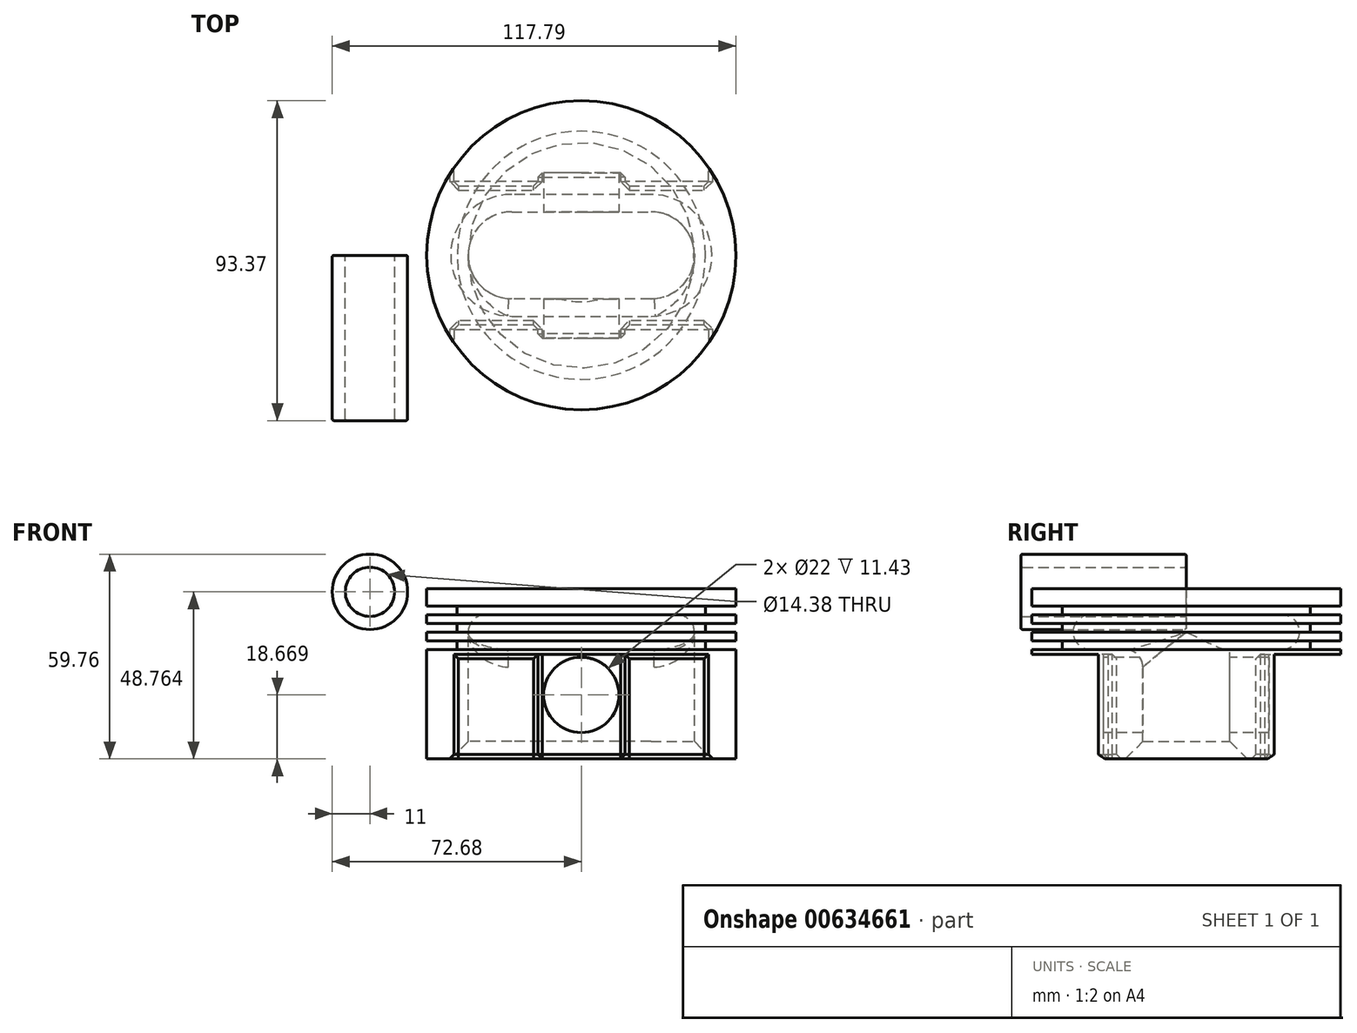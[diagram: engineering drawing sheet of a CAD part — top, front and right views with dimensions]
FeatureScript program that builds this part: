
annotation { "Feature Type Name" : "Feature", "Feature Type Description" : "" }
export const myFeature = defineFeature(function(context is Context, id is Id, definition is map)
    precondition{}
    {
        {
            var Q0;
            Q0=qCreatedBy(makeId("Front.planeOp"),FACE);
            var sketch = newSketch(context, id + "F0", { "sketchPlane" : qUnion([Q0])});
            skLineSegment(sketch, "E0", {"start": v(0, 30.06) * mm, "end": v(-45.11, 30.06) * mm});
            skLineSegment(sketch, "E1", {"start": v(-45.11, 30.06) * mm, "end": v(-45.11, 24.98) * mm});
            skLineSegment(sketch, "E2", {"start": v(-45.11, 24.98) * mm, "end": v(-36.22, 24.98) * mm});
            skLineSegment(sketch, "E3", {"start": v(-36.22, 24.98) * mm, "end": v(-36.22, 22.44) * mm});
            skLineSegment(sketch, "E4", {"start": v(-36.22, 22.44) * mm, "end": v(-45.11, 22.44) * mm});
            skLineSegment(sketch, "E5", {"start": v(-45.11, 22.44) * mm, "end": v(-45.11, 19.9) * mm});
            skLineSegment(sketch, "E6", {"start": v(-45.11, 19.9) * mm, "end": v(-36.22, 19.9) * mm});
            skLineSegment(sketch, "E7", {"start": v(-36.22, 19.9) * mm, "end": v(-36.22, 17.36) * mm});
            skLineSegment(sketch, "E8", {"start": v(-36.22, 17.36) * mm, "end": v(-45.11, 17.36) * mm});
            skLineSegment(sketch, "E9", {"start": v(-45.11, 17.36) * mm, "end": v(-45.11, 14.82) * mm});
            skLineSegment(sketch, "E10", {"start": v(-45.11, 14.82) * mm, "end": v(-36.22, 14.82) * mm});
            skLineSegment(sketch, "E11", {"start": v(-45.11, 10.86) * mm, "end": v(-45.11, -0.67) * mm});
            skLineSegment(sketch, "E12", {"start": v(-45.11, 10.86) * mm, "end": v(0, 10.86) * mm});
            skLineSegment(sketch, "E13", {"start": v(-36.22, 14.82) * mm, "end": v(-36.22, 12.28) * mm});
            skLineSegment(sketch, "E14", {"start": v(-36.22, 12.28) * mm, "end": v(-45.11, 12.28) * mm});
            skLineSegment(sketch, "E15", {"start": v(-45.11, 12.28) * mm, "end": v(-45.11, 10.86) * mm});
            skLineSegment(sketch, "E16", {"start": v(0, 30.06) * mm, "end": v(0, 22.44) * mm});
            skLineSegment(sketch, "E17", {"start": v(0, 22.44) * mm, "end": v(-27.94, 22.44) * mm});
            skLineSegment(sketch, "E18", {"start": v(0, 0) * mm, "end": v(0, 12.28) * mm});
            skLineSegment(sketch, "E19", {"start": v(0, 12.28) * mm, "end": v(-27.94, 12.28) * mm});
            skArc(sketch, "E20", {"start": v(-27.94, 22.44) * mm, "mid": v(-33.02, 17.36) * mm, "end": v(-27.94, 12.28) * mm});
            skLineSegment(sketch, "E21", {"start": v(0, 0.32) * mm, "end": v(0, 10.86) * mm});
            skCircle(sketch, "E22", {"center": v(0, -0.95) * mm, "radius": 11 * mm, "construction": true});
            skSolve(sketch);
        }
        {
            var Q0;
            Q0=makeQuery(id+"F0.imprint","IMPRINT",FACE,{"disambiguationData":[TD([[makeQuery(id+"F0.imprint","IMPRINT",EDGE,{"derivedFrom":sQuery(id+"F0.wireOp",EDGE,"E0")}),1.0]])]});
            var Q1;
            Q1=sQuery(id+"F0.wireOp",EDGE,"E18");
            revolve(context, id + "F1", {"entities" : qUnion([Q0]), "axis" : qUnion([Q1]), "revolveType" : RevolveType.FULL});
        }
        {
            var Q0;
            Q0=makeQuery(id+"F1.opRevolve","SWEPT_FACE",FACE,{"disambiguationData":[OSD([sQuery(id+"F0.wireOp",EDGE,"E12")])]});
            var sketch = newSketch(context, id + "F2", { "sketchPlane" : qUnion([Q0])});
            skLineSegment(sketch, "E23", {"start": v(0, 12.7) * mm, "end": v(-20.32, 12.7) * mm});
            skLineSegment(sketch, "E24.MirrorCS", {"start": v(0, -12.7) * mm, "end": v(-20.32, -12.7) * mm});
            skArc(sketch, "E25", {"start": v(-20.32, 12.7) * mm, "mid": v(-33.02, 0) * mm, "end": v(-20.32, -12.7) * mm});
            skLineSegment(sketch, "E26.MirrorCS", {"start": v(0, 12.7) * mm, "end": v(20.32, 12.7) * mm});
            skArc(sketch, "E27.MirrorCS", {"start": v(20.32, 12.7) * mm, "mid": v(33.02, 0) * mm, "end": v(20.32, -12.7) * mm});
            skLineSegment(sketch, "E28.MirrorCS", {"start": v(0, -12.7) * mm, "end": v(20.32, -12.7) * mm});
            skLineSegment(sketch, "E29", {"start": v(-12.7, 20.32) * mm, "end": v(-37.13, 20.32) * mm});
            skLineSegment(sketch, "E30", {"start": v(-37.13, 20.32) * mm, "end": v(-37.13, 25.61) * mm});
            skLineSegment(sketch, "E31", {"start": v(0, 24.13) * mm, "end": v(-12.7, 24.13) * mm});
            skLineSegment(sketch, "E32", {"start": v(-12.7, 24.13) * mm, "end": v(-12.7, 20.32) * mm});
            skPoint(sketch, "E33.orphan", {"position": v(0, 20.32) * mm});
            skLineSegment(sketch, "E34.MirrorCS", {"start": v(12.7, 24.13) * mm, "end": v(12.7, 20.32) * mm});
            skLineSegment(sketch, "E35.MirrorCS", {"start": v(37.13, 20.32) * mm, "end": v(37.13, 25.61) * mm});
            skLineSegment(sketch, "E36.MirrorCS", {"start": v(0, 24.13) * mm, "end": v(12.7, 24.13) * mm});
            skLineSegment(sketch, "E37.MirrorCS", {"start": v(12.7, 20.32) * mm, "end": v(37.13, 20.32) * mm});
            skLineSegment(sketch, "E38.MirrorCS", {"start": v(12.7, -24.13) * mm, "end": v(12.7, -20.32) * mm});
            skLineSegment(sketch, "E39.MirrorCS", {"start": v(-12.7, -24.13) * mm, "end": v(-12.7, -20.32) * mm});
            skPoint(sketch, "E40.MirrorP", {"position": v(0, -20.32) * mm});
            skLineSegment(sketch, "E41.MirrorCS", {"start": v(-12.7, -20.32) * mm, "end": v(-37.13, -20.32) * mm});
            skLineSegment(sketch, "E42.MirrorCS", {"start": v(12.7, -20.32) * mm, "end": v(37.13, -20.32) * mm});
            skLineSegment(sketch, "E43.MirrorCS", {"start": v(-37.13, -20.32) * mm, "end": v(-37.13, -25.61) * mm});
            skLineSegment(sketch, "E44.MirrorCS", {"start": v(0, -24.13) * mm, "end": v(12.7, -24.13) * mm});
            skLineSegment(sketch, "E45.MirrorCS", {"start": v(37.13, -20.32) * mm, "end": v(37.13, -25.61) * mm});
            skLineSegment(sketch, "E46.MirrorCS", {"start": v(0, -24.13) * mm, "end": v(-12.7, -24.13) * mm});
            skSolve(sketch);
        }
        {
            var Q0;
            Q0=makeQuery(id+"F2.imprint","IMPRINT",FACE,{"disambiguationData":[TD([[makeQuery(id+"F2.imprint","IMPRINT",EDGE,{"derivedFrom":sQuery(id+"F2.wireOp",EDGE,"E23")}),-1.0]])]});
            extrude(context, id + "F3", {"entities" : qUnion([Q0]), "operationType" : NewBodyOperationType.ADD, "depth" : 30.48 * mm, "offsetDistance" : 25.4 * mm});
        }
        {
            var Q0;
            Q0=makeQuery(id+"F3.opExtrude","SWEPT_FACE",FACE,{"disambiguationData":[OSD([sQuery(id+"F2.wireOp",EDGE,"E31"),sQuery(id+"F2.wireOp",EDGE,"E36.MirrorCS")])]});
            var sketch = newSketch(context, id + "F4", { "sketchPlane" : qUnion([Q0])});
            skCircle(sketch, "E47", {"center": v(0, -0.95) * mm, "radius": 11 * mm});
            skSolve(sketch);
        }
        {
            var Q0;
            Q0 = qSketchRegion(id + "F4", true);
            extrude(context, id + "F5", {"entities" : qUnion([Q0]), "operationType" : NewBodyOperationType.REMOVE, "oppositeDirection" : true, "depth" : 156.46 * mm, "offsetDistance" : 25.4 * mm, "symmetric" : true});
        }
        {
            var Q0;
            Q0=makeQuery(id+"F3.opExtrude","CAP_EDGE",EDGE,{"disambiguationData":[OSD([sQuery(id+"F2.wireOp",EDGE,"E25")])],"isStart":false});
            chamfer(context, id + "F6", {"entities" : qUnion([Q0]), "width" : 5.08 * mm, "tangentPropagation" : true});
        }
        {
            var Q0;
            Q0=makeQuery(id+"F3.opExtrude","SWEPT_FACE",FACE,{"disambiguationData":[OSD([sQuery(id+"F2.wireOp",EDGE,"E29")])]});
            var Q1;
            Q1=makeQuery(id+"F3.opExtrude","SWEPT_FACE",FACE,{"disambiguationData":[OSD([sQuery(id+"F2.wireOp",EDGE,"E37.MirrorCS")])]});
            var Q2;
            Q2=makeQuery(id+"F3.opExtrude","SWEPT_EDGE",EDGE,{"disambiguationData":[OSD([sQuery(id+"F2.wireOp",EDGE,"E34.MirrorCS"),sQuery(id+"F2.wireOp",EDGE,"E36.MirrorCS")])]});
            var Q3;
            Q3=makeQuery(id+"F3.opExtrude","SWEPT_EDGE",EDGE,{"disambiguationData":[OSD([sQuery(id+"F2.wireOp",EDGE,"E31"),sQuery(id+"F2.wireOp",EDGE,"E32")])]});
            var Q4;
            Q4=makeQuery(id+"F3.opExtrude","CAP_EDGE",EDGE,{"disambiguationData":[OSD([sQuery(id+"F2.wireOp",EDGE,"E31"),sQuery(id+"F2.wireOp",EDGE,"E36.MirrorCS")])],"isStart":true});
            var Q5;
            Q5=makeQuery(id+"F3.opExtrude","CAP_EDGE",EDGE,{"disambiguationData":[OSD([sQuery(id+"F2.wireOp",EDGE,"E31"),sQuery(id+"F2.wireOp",EDGE,"E36.MirrorCS")])],"isStart":false});
            var Q6;
            Q6=makeQuery(id+"F3.opExtrude","SWEPT_FACE",FACE,{"disambiguationData":[OSD([sQuery(id+"F2.wireOp",EDGE,"E41.MirrorCS")])]});
            var Q7;
            Q7=makeQuery(id+"F3.opExtrude","SWEPT_FACE",FACE,{"disambiguationData":[OSD([sQuery(id+"F2.wireOp",EDGE,"E42.MirrorCS")])]});
            var Q8;
            Q8=makeQuery(id+"F3.opExtrude","CAP_EDGE",EDGE,{"disambiguationData":[OSD([sQuery(id+"F2.wireOp",EDGE,"E44.MirrorCS"),sQuery(id+"F2.wireOp",EDGE,"E46.MirrorCS")])],"isStart":false});
            var Q9;
            Q9=makeQuery(id+"F3.opExtrude","SWEPT_EDGE",EDGE,{"disambiguationData":[OSD([sQuery(id+"F2.wireOp",EDGE,"E38.MirrorCS"),sQuery(id+"F2.wireOp",EDGE,"E44.MirrorCS")])]});
            var Q10;
            Q10=makeQuery(id+"F3.opExtrude","SWEPT_EDGE",EDGE,{"disambiguationData":[OSD([sQuery(id+"F2.wireOp",EDGE,"E39.MirrorCS"),sQuery(id+"F2.wireOp",EDGE,"E46.MirrorCS")])]});
            var Q11;
            Q11=makeQuery(id+"F3.opExtrude","CAP_EDGE",EDGE,{"disambiguationData":[OSD([sQuery(id+"F2.wireOp",EDGE,"E44.MirrorCS"),sQuery(id+"F2.wireOp",EDGE,"E46.MirrorCS")])],"isStart":true});
            chamfer(context, id + "F7", {"entities" : qUnion([Q0, Q1, Q2, Q3, Q4, Q5, Q6, Q7, Q8, Q9, Q10, Q11]), "width" : 1.27 * mm, "tangentPropagation" : true});
        }
        {
            var Q0;
            Q0=makeQuery(id+"F3.boolean.opBoolean","SPLIT",FACE,{"disambiguationData":[TD([makeQuery(id+"F3.opExtrude","SWEPT_FACE",FACE,{"disambiguationData":[OSD([sQuery(id+"F2.wireOp",EDGE,"E25")])]})])],"derivedFrom":makeQuery(id+"F1.opRevolve","SWEPT_FACE",FACE,{"disambiguationData":[OSD([sQuery(id+"F0.wireOp",EDGE,"E12")])]})});
            extrude(context, id + "F8", {"entities" : qUnion([Q0]), "operationType" : NewBodyOperationType.REMOVE, "oppositeDirection" : true, "depth" : 6.35 * mm, "offsetDistance" : 25.4 * mm});
        }
        {
            var Q0;
            Q0=makeQuery(id+"F8.boolean.opBoolean","INTERSECT",EDGE,{"disambiguationData":[OD(0.0)],"derivedFrom":[makeQuery(id+"F1.opRevolve","SWEPT_FACE",FACE,{"disambiguationData":[OSD([sQuery(id+"F0.wireOp",EDGE,"E20")])]}),makeQuery(id+"F8.opExtrude","SWEPT_FACE",FACE,{"disambiguationData":[OSD([sQuery(id+"F2.wireOp",EDGE,"E25")])]})]});
            fillet(context, id + "F9", {"entities" : qUnion([Q0]), "radius" : 5.08 * mm, "tangentPropagation" : true, "allowEdgeOverflow" : false});
        }
        {
            var Q0;
            Q0=qCreatedBy(makeId("Front.planeOp"),FACE);
            var sketch = newSketch(context, id + "F10", { "sketchPlane" : qUnion([Q0])});
            skCircle(sketch, "E48", {"center": v(-61.68, 29.14) * mm, "radius": 11 * mm});
            skCircle(sketch, "E49.0", {"center": v(-61.68, 29.14) * mm, "radius": 7.19 * mm});
            skSolve(sketch);
        }
        {
            var Q0;
            Q0=makeQuery(id+"F10.imprint","IMPRINT",FACE,{"disambiguationData":[TD([[makeQuery(id+"F10.imprint","IMPRINT",EDGE,{"derivedFrom":sQuery(id+"F10.wireOp",EDGE,"E48")}),1.0]])]});
            extrude(context, id + "F11", {"entities" : qUnion([Q0]), "depth" : 48.26 * mm, "offsetDistance" : 25.4 * mm});
        }
        {
            var Q0;
            Q0=makeQuery(id+"F11.opExtrude","CAP_FACE",FACE,{"disambiguationData":[OSD([sQuery(id+"F10.wireOp",EDGE,"E48"),sQuery(id+"F10.wireOp",EDGE,"E49.0")])],"isStart":false});
            var Q1;
            Q1=makeQuery(id+"F11.opExtrude","CAP_FACE",FACE,{"disambiguationData":[OSD([sQuery(id+"F10.wireOp",EDGE,"E48"),sQuery(id+"F10.wireOp",EDGE,"E49.0")])],"isStart":true});
            fillet(context, id + "F12", {"entities" : qUnion([Q0, Q1]), "radius" : 0.5 * mm, "tangentPropagation" : true, "allowEdgeOverflow" : false});
        }
    });
